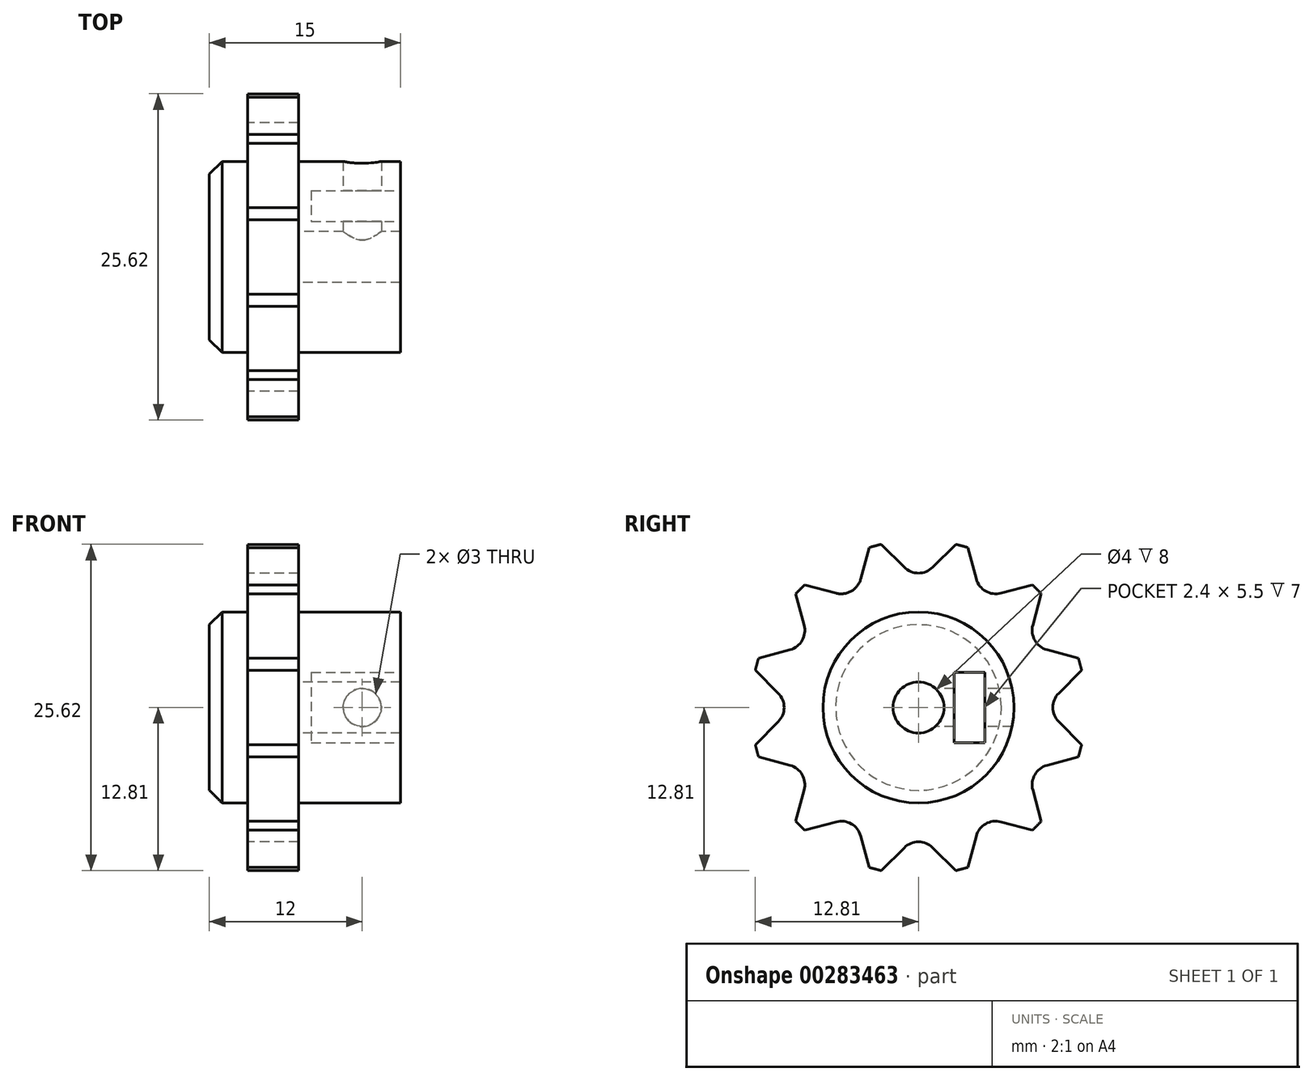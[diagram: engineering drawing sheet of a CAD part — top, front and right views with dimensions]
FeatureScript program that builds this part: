
annotation { "Feature Type Name" : "Feature", "Feature Type Description" : "" }
export const myFeature = defineFeature(function(context is Context, id is Id, definition is map)
    precondition{}
    {
        {
            var Q0;
            Q0=qCreatedBy(makeId("Right.planeOp"),FACE);
            var sketch = newSketch(context, id + "F0", { "sketchPlane" : qUnion([Q0])});
            skCircle(sketch, "E0", {"center": v(0, 0) * mm, "radius": 2 * mm});
            skCircle(sketch, "E1", {"center": v(0, 0) * mm, "radius": 7.5 * mm});
            skArc(sketch, "E2", {"start": v(-2.92, 12.8) * mm, "mid": v(0, -13.13) * mm, "end": v(2.92, 12.8) * mm});
            skArc(sketch, "E3", {"start": v(-1.12, 11.01) * mm, "mid": v(0, 10.55) * mm, "end": v(1.12, 11.01) * mm});
            skLineSegment(sketch, "E4", {"start": v(1.12, 11.01) * mm, "end": v(2.92, 12.8) * mm});
            skLineSegment(sketch, "E5", {"start": v(-1.12, 11.01) * mm, "end": v(-2.92, 12.8) * mm});
            skLineSegment(sketch, "E6.1.0", {"start": v(-6.48, 8.98) * mm, "end": v(-8.93, 9.63) * mm});
            skArc(sketch, "E6.1.1", {"start": v(-6.48, 8.98) * mm, "mid": v(-5.27, 9.13) * mm, "end": v(-4.53, 10.1) * mm});
            skLineSegment(sketch, "E6.1.2", {"start": v(-4.53, 10.1) * mm, "end": v(-3.88, 12.55) * mm});
            skLineSegment(sketch, "E6.2.0", {"start": v(-10.1, 4.53) * mm, "end": v(-12.55, 3.88) * mm});
            skArc(sketch, "E6.2.1", {"start": v(-10.1, 4.53) * mm, "mid": v(-9.13, 5.27) * mm, "end": v(-8.98, 6.48) * mm});
            skLineSegment(sketch, "E6.2.2", {"start": v(-8.98, 6.48) * mm, "end": v(-9.63, 8.93) * mm});
            skLineSegment(sketch, "E6.3.0", {"start": v(-11.01, -1.12) * mm, "end": v(-12.8, -2.92) * mm});
            skArc(sketch, "E6.3.1", {"start": v(-11.01, -1.12) * mm, "mid": v(-10.55, 0) * mm, "end": v(-11.01, 1.12) * mm});
            skLineSegment(sketch, "E6.3.2", {"start": v(-11.01, 1.12) * mm, "end": v(-12.8, 2.92) * mm});
            skLineSegment(sketch, "E6.4.0", {"start": v(-8.98, -6.48) * mm, "end": v(-9.63, -8.93) * mm});
            skArc(sketch, "E6.4.1", {"start": v(-8.98, -6.48) * mm, "mid": v(-9.13, -5.27) * mm, "end": v(-10.1, -4.53) * mm});
            skLineSegment(sketch, "E6.4.2", {"start": v(-10.1, -4.53) * mm, "end": v(-12.55, -3.88) * mm});
            skLineSegment(sketch, "E6.5.0", {"start": v(-4.53, -10.1) * mm, "end": v(-3.88, -12.55) * mm});
            skArc(sketch, "E6.5.1", {"start": v(-4.53, -10.1) * mm, "mid": v(-5.27, -9.13) * mm, "end": v(-6.48, -8.98) * mm});
            skLineSegment(sketch, "E6.5.2", {"start": v(-6.48, -8.98) * mm, "end": v(-8.93, -9.63) * mm});
            skLineSegment(sketch, "E6.6.0", {"start": v(1.12, -11.01) * mm, "end": v(2.92, -12.8) * mm});
            skArc(sketch, "E6.6.1", {"start": v(1.12, -11.01) * mm, "mid": v(0, -10.55) * mm, "end": v(-1.12, -11.01) * mm});
            skLineSegment(sketch, "E6.6.2", {"start": v(-1.12, -11.01) * mm, "end": v(-2.92, -12.8) * mm});
            skLineSegment(sketch, "E6.7.0", {"start": v(6.48, -8.98) * mm, "end": v(8.93, -9.63) * mm});
            skArc(sketch, "E6.7.1", {"start": v(6.48, -8.98) * mm, "mid": v(5.27, -9.13) * mm, "end": v(4.53, -10.1) * mm});
            skLineSegment(sketch, "E6.7.2", {"start": v(4.53, -10.1) * mm, "end": v(3.88, -12.55) * mm});
            skLineSegment(sketch, "E6.8.0", {"start": v(10.1, -4.53) * mm, "end": v(12.55, -3.88) * mm});
            skArc(sketch, "E6.8.1", {"start": v(10.1, -4.53) * mm, "mid": v(9.13, -5.27) * mm, "end": v(8.98, -6.48) * mm});
            skLineSegment(sketch, "E6.8.2", {"start": v(8.98, -6.48) * mm, "end": v(9.63, -8.93) * mm});
            skLineSegment(sketch, "E6.9.0", {"start": v(11.01, 1.12) * mm, "end": v(12.8, 2.92) * mm});
            skArc(sketch, "E6.9.1", {"start": v(11.01, 1.12) * mm, "mid": v(10.55, 0) * mm, "end": v(11.01, -1.12) * mm});
            skLineSegment(sketch, "E6.9.2", {"start": v(11.01, -1.12) * mm, "end": v(12.8, -2.92) * mm});
            skLineSegment(sketch, "E6.10.0", {"start": v(8.98, 6.48) * mm, "end": v(9.63, 8.93) * mm});
            skArc(sketch, "E6.10.1", {"start": v(8.98, 6.48) * mm, "mid": v(9.13, 5.27) * mm, "end": v(10.1, 4.53) * mm});
            skLineSegment(sketch, "E6.10.2", {"start": v(10.1, 4.53) * mm, "end": v(12.55, 3.88) * mm});
            skLineSegment(sketch, "E6.11.0", {"start": v(4.53, 10.1) * mm, "end": v(3.88, 12.55) * mm});
            skArc(sketch, "E6.11.1", {"start": v(4.53, 10.1) * mm, "mid": v(5.27, 9.13) * mm, "end": v(6.48, 8.98) * mm});
            skLineSegment(sketch, "E6.11.2", {"start": v(6.48, 8.98) * mm, "end": v(8.93, 9.63) * mm});
            skSolve(sketch);
        }
        {
            var Q0;
            Q0=makeQuery(id+"F0.imprint","IMPRINT",FACE,{"disambiguationData":[TD([[makeQuery(id+"F0.imprint","IMPRINT",EDGE,{"derivedFrom":sQuery(id+"F0.wireOp",EDGE,"E0")}),-1.0]])]});
            extrude(context, id + "F1", {"entities" : qUnion([Q0]), "depth" : 12 * mm, "hasSecondDirection" : true, "secondDirectionOppositeDirection" : true, "secondDirectionDepth" : 3 * mm});
        }
        {
            var Q0;
            Q0=makeQuery(id+"F0.imprint","IMPRINT",FACE,{"disambiguationData":[TD([[makeQuery(id+"F0.imprint","IMPRINT",EDGE,{"derivedFrom":sQuery(id+"F0.wireOp",EDGE,"E1")}),-1.0]])]});
            var Q1;
            Q1=makeQuery(id+"F0.imprint","IMPRINT",FACE,{"disambiguationData":[TD([[makeQuery(id+"F0.imprint","IMPRINT",EDGE,{"derivedFrom":sQuery(id+"F0.wireOp",EDGE,"E0")}),1.0]])]});
            extrude(context, id + "F2", {"entities" : qUnion([Q0, Q1]), "operationType" : NewBodyOperationType.ADD, "depth" : 4 * mm});
        }
        {
            var Q0;
            Q0=makeQuery(id+"F2.opExtrude","CAP_FACE",FACE,{"disambiguationData":[OSD([sQuery(id+"F0.wireOp",EDGE,"E0")])],"isStart":true});
            extrude(context, id + "F3", {"entities" : qUnion([Q0]), "operationType" : NewBodyOperationType.ADD, "depth" : 3 * mm});
        }
        {
            var Q0;
            Q0=makeQuery(id+"F1.opExtrude","CAP_EDGE",EDGE,{"disambiguationData":[OSD([sQuery(id+"F0.wireOp",EDGE,"E1")])],"isStart":true});
            chamfer(context, id + "F4", {"entities" : qUnion([Q0]), "width" : 1 * mm, "tangentPropagation" : true});
        }
        {
            var Q0;
            Q0=makeQuery(id+"F1.opExtrude","CAP_FACE",FACE,{"disambiguationData":[OSD([sQuery(id+"F0.wireOp",EDGE,"E0"),sQuery(id+"F0.wireOp",EDGE,"E1")])],"isStart":false});
            var sketch = newSketch(context, id + "F5", { "sketchPlane" : qUnion([Q0])});
            skLineSegment(sketch, "E7.bottom", {"start": v(5.2, 2.75) * mm, "end": v(2.8, 2.75) * mm});
            skLineSegment(sketch, "E7.top", {"start": v(5.2, -2.75) * mm, "end": v(2.8, -2.75) * mm});
            skLineSegment(sketch, "E7.left", {"start": v(5.2, 2.75) * mm, "end": v(5.2, -2.75) * mm});
            skLineSegment(sketch, "E7.right", {"start": v(2.8, 2.75) * mm, "end": v(2.8, -2.75) * mm});
            skPoint(sketch, "E7.middle", {"position": v(4, 0) * mm});
            skSolve(sketch);
        }
        {
            var Q0;
            Q0=makeQuery(id+"F5.imprint","IMPRINT",FACE,{"disambiguationData":[TD([[makeQuery(id+"F5.imprint","IMPRINT",EDGE,{"derivedFrom":sQuery(id+"F5.wireOp",EDGE,"E7.bottom")}),1.0]])]});
            extrude(context, id + "F6", {"entities" : qUnion([Q0]), "operationType" : NewBodyOperationType.REMOVE, "oppositeDirection" : true, "depth" : 7 * mm});
        }
        {
            var Q0;
            Q0=makeQuery(id+"F6.boolean.opBoolean","COPY",FACE,{"derivedFrom":makeQuery(id+"F6.opExtrude","SWEPT_FACE",FACE,{"disambiguationData":[OSD([sQuery(id+"F5.wireOp",EDGE,"E7.right")])]})});
            var sketch = newSketch(context, id + "F7", { "sketchPlane" : qUnion([Q0])});
            skCircle(sketch, "E8", {"center": v(-9, 0) * mm, "radius": 1.5 * mm});
            skPoint(sketch, "E8.centerSnap0", {"position": v(-12, 0) * mm});
            skSolve(sketch);
        }
        {
            var Q0;
            Q0=makeQuery(id+"F7.imprint","IMPRINT",FACE,{"disambiguationData":[TD([[makeQuery(id+"F7.imprint","IMPRINT",EDGE,{"derivedFrom":sQuery(id+"F7.wireOp",EDGE,"E8")}),1.0]])]});
            extrude(context, id + "F8", {"entities" : qUnion([Q0]), "operationType" : NewBodyOperationType.REMOVE, "endBound" : BoundingType.THROUGH_ALL, "depth" : 3 * mm, "hasSecondDirection" : true, "secondDirectionBound" : SecondDirectionBoundingType.UP_TO_NEXT, "secondDirectionOppositeDirection" : true, "secondDirectionDepth" : 25 * mm});
        }
    });
